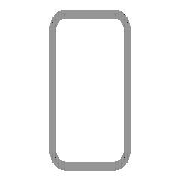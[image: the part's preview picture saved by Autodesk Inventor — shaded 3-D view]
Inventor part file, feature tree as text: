
AUTODESK INVENTOR PART (.ipt)
format: ipt  version: 2025 (Build 290162010, 162A)  size: 137,728 bytes
history: native  units: mm (DEFAULTED — no unit token found)
features: other x3, sketch x1, plane x1
ambient origin geometry x8: Origin, YZ Plane, XZ Plane, XY Plane, X Axis, Y Axis, Z Axis, Center Point
bodies: Solid1 (feature_tree), Body (feature_tree)
feature tree (5):
  other  "Driven Length"
  other  "Start plane"
  other  "End plane"
  sketch  "Sketch3"  dims[d3=7000.0mm d4=0.0mm d7=4.5mm d10=80.0mm d11=40.0mm d12=3.0mm d13=-0.0mm d14=7000.0mm d15=40.0mm d16=20.0mm d17=90.0deg d18=7000.0mm d19=3.0mm d20=3.0mm]
  plane  "Work Plane3"
